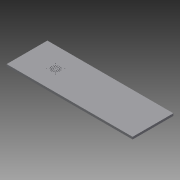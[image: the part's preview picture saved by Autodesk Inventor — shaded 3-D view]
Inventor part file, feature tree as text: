
AUTODESK INVENTOR PART (.ipt)
format: ipt  version: 2015 SP1 (Build 190203100, 203)  size: 147,968 bytes
history: native  units: mm
features: extrude x2, sketch x2, hole x1, pattern_linear x1
ambient origin geometry x8: Origin, YZ Plane, XZ Plane, XY Plane, X Axis, Y Axis, Z Axis, Center Point
bodies: Solid1 (feature_tree)
feature tree (6):
  extrude  "Extrusion1"  Depth=144.0mm
  hole  "Hole1"  [1 undecoded]
  pattern_linear  "Rectangular Pattern1"  Spacing1=8.0mm  [1 undecoded]
  extrude  "Extrusion2"  Depth=8.0mm
  sketch  "Sketch1"  dims[d0=445.0mm d1=144.0mm]
  sketch  "Sketch2"  dims[d2=72.0mm d3=222.5mm d4=8.0mm d5=0.0mm d6=85.0mm d7=88.0mm d8=3.0mm d9=6.0mm d10=4.0mm d11=2.0mm d12=90.0deg d13=8.0mm d14=20.594885mm d15=20.0mm d17=32.0mm d18=20.0mm d20=32.0mm d21=3.0mm d22=101.0mm d23=3.0mm d24=6.0mm d25=60.0mm d27=360.0deg d29=3.0mm d30=10.0mm d31=120.0mm d33=360.0deg d35=3.0mm d36=14.0mm d37=160.0mm d39=360.0deg d41=8.0mm d42=0.0mm]
note: 2 required parameter values undecoded (feature->parameter linkage not recoverable at this tier; creation-order binding heuristic only, values carry confidence <= 0.55)
